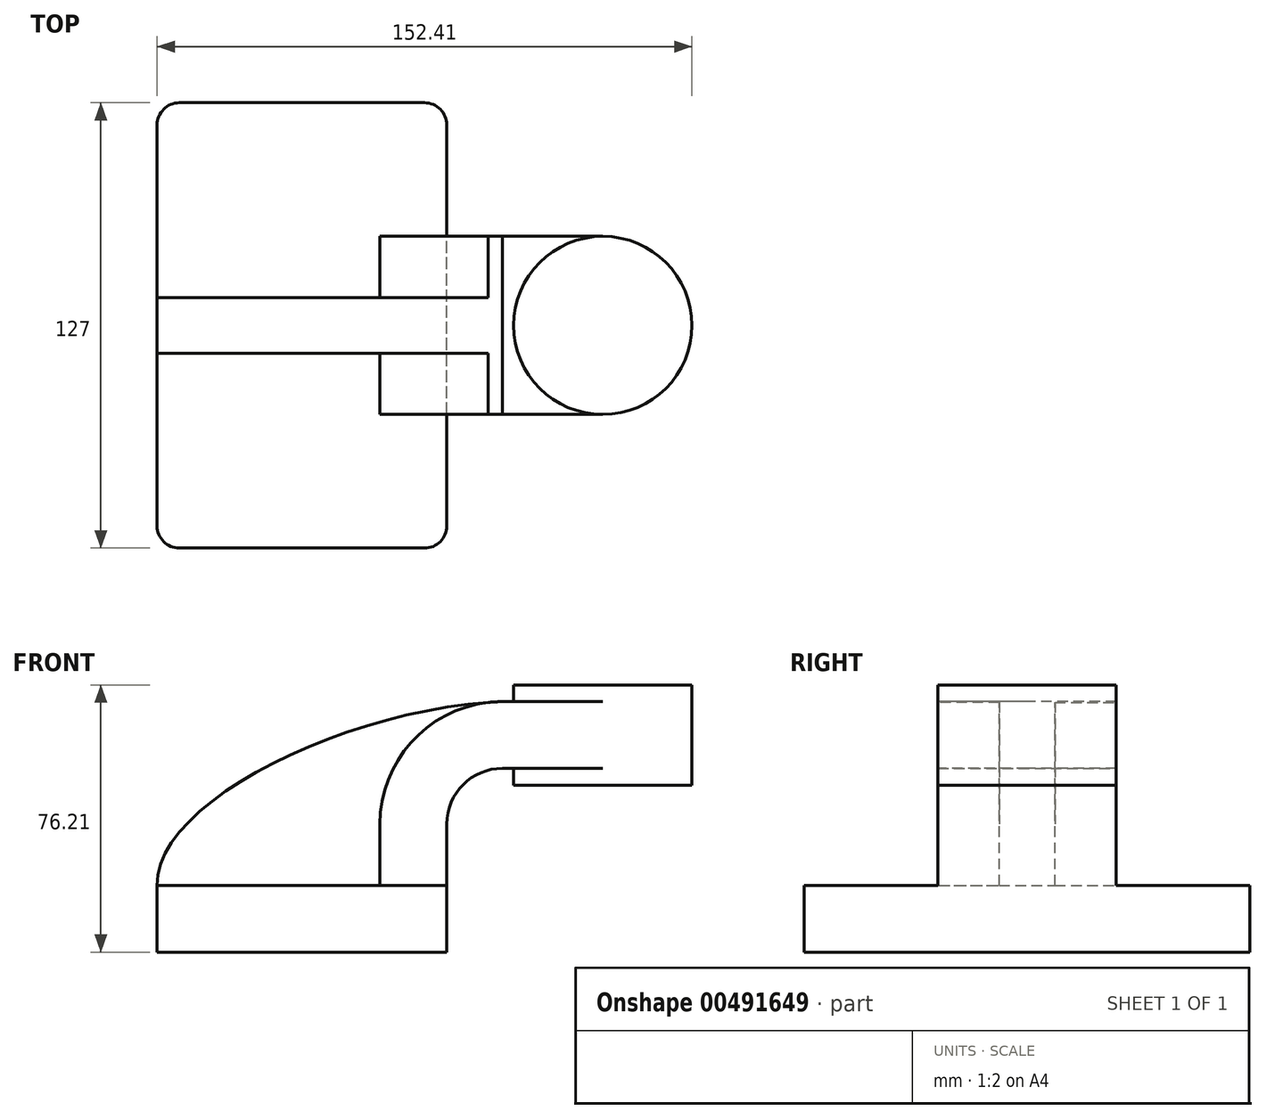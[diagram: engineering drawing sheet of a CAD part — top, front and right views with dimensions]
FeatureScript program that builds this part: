
annotation { "Feature Type Name" : "Feature", "Feature Type Description" : "" }
export const myFeature = defineFeature(function(context is Context, id is Id, definition is map)
    precondition{}
    {
        {
            var Q0;
            Q0=qCreatedBy(makeId("Front.planeOp"),FACE);
            var sketch = newSketch(context, id + "F0", { "sketchPlane" : qUnion([Q0])});
            skLineSegment(sketch, "E0.bottom", {"start": v(-41.28, 9.52) * mm, "end": v(41.27, 9.53) * mm});
            skLineSegment(sketch, "E0.top", {"start": v(-41.28, -9.53) * mm, "end": v(41.28, -9.53) * mm});
            skLineSegment(sketch, "E0.left", {"start": v(-41.28, 9.52) * mm, "end": v(-41.28, -9.53) * mm});
            skLineSegment(sketch, "E0.right", {"start": v(41.27, 9.53) * mm, "end": v(41.28, -9.52) * mm});
            skPoint(sketch, "E0.middle", {"position": v(0, 0) * mm});
            skLineSegment(sketch, "E1.bottom", {"start": v(60.32, 38.1) * mm, "end": v(111.12, 38.1) * mm});
            skLineSegment(sketch, "E1.top", {"start": v(60.32, 66.68) * mm, "end": v(111.12, 66.68) * mm});
            skLineSegment(sketch, "E1.left", {"start": v(60.32, 38.1) * mm, "end": v(60.32, 66.68) * mm});
            skLineSegment(sketch, "E1.right", {"start": v(111.12, 38.1) * mm, "end": v(111.12, 66.68) * mm});
            skPoint(sketch, "E1.middle", {"position": v(85.72, 52.39) * mm});
            skLineSegment(sketch, "E2", {"start": v(41.27, 9.53) * mm, "end": v(41.27, 27) * mm});
            skArc(sketch, "E3", {"start": v(41.27, 27) * mm, "mid": v(45.92, 38.23) * mm, "end": v(57.15, 42.88) * mm});
            skLineSegment(sketch, "E4", {"start": v(57.15, 42.88) * mm, "end": v(85.72, 42.88) * mm});
            skPoint(sketch, "E4.endSnap0", {"position": v(85.72, 38.1) * mm});
            skLineSegment(sketch, "E5.0", {"start": v(57.15, 61.93) * mm, "end": v(85.72, 61.93) * mm});
            skArc(sketch, "E5.1", {"start": v(22.22, 27) * mm, "mid": v(32.45, 51.7) * mm, "end": v(57.15, 61.93) * mm});
            skLineSegment(sketch, "E5.2", {"start": v(22.22, 9.53) * mm, "end": v(22.22, 27) * mm});
            skLineSegment(sketch, "E6", {"start": v(85.72, 38.1) * mm, "end": v(85.72, 66.68) * mm});
            skFitSpline(sketch, "E7", {"points": [v(-41.28, 9.52) * mm, v(57.15, 61.93) * mm], "startDerivative": vector(-1.75, 71.36) * mm, "endDerivative": vector(133.88, 5.67) * mm});
            skSolve(sketch);
        }
        {
            var Q0;
            Q0=makeQuery(id+"F0.imprint","IMPRINT",FACE,{"disambiguationData":[TD([[makeQuery(id+"F0.imprint","IMPRINT",EDGE,{"derivedFrom":sQuery(id+"F0.wireOp",EDGE,"E0.top")}),1.0]])]});
            extrude(context, id + "F1", {"entities" : qUnion([Q0]), "endBound" : BoundingType.SYMMETRIC, "depth" : 127 * mm});
        }
        {
            var Q0;
            {var subQ1=sQuery(id+"F0.wireOp",EDGE,"E2");Q0=makeQuery(id+"F0.imprint","IMPRINT",FACE,{"disambiguationData":[TD([[makeQuery(id+"F0.imprint","IMPRINT",EDGE,{"derivedFrom":subQ1}),1.0]])]});}
            var Q1;
            {var subQ0=sQuery(id+"F0.wireOp",EDGE,"E4");var subQ1=sQuery(id+"F0.wireOp",EDGE,"E1.left");var subQ2=makeQuery(id+"F0.imprint","INTERSECT",VERTEX,{"derivedFrom":[subQ1,subQ0]});Q1=makeQuery(id+"F0.imprint","IMPRINT",FACE,{"disambiguationData":[TD([[makeQuery(id+"F0.imprint","IMPRINT",EDGE,{"disambiguationData":[TD([[subQ2,-1.0]])],"derivedFrom":subQ1}),-1.0]])]});}
            extrude(context, id + "F2", {"entities" : qUnion([Q0, Q1]), "operationType" : NewBodyOperationType.ADD, "endBound" : BoundingType.SYMMETRIC, "depth" : 50.8 * mm});
        }
        {
            var Q0;
            {var subQ3=sQuery(id+"F0.wireOp",EDGE,"E5.2");Q0=makeQuery(id+"F0.imprint","IMPRINT",FACE,{"disambiguationData":[TD([[makeQuery(id+"F0.imprint","IMPRINT",EDGE,{"derivedFrom":subQ3}),1.0]])]});}
            extrude(context, id + "F3", {"entities" : qUnion([Q0]), "operationType" : NewBodyOperationType.ADD, "endBound" : BoundingType.SYMMETRIC, "depth" : 15.88 * mm});
        }
        {
            var Q0;
            {var subQ4=sQuery(id+"F0.wireOp",EDGE,"E1.right");Q0=makeQuery(id+"F0.imprint","IMPRINT",FACE,{"disambiguationData":[TD([[makeQuery(id+"F0.imprint","IMPRINT",EDGE,{"derivedFrom":subQ4}),1.0]])]});}
            var Q1;
            Q1=sQuery(id+"F0.wireOp",EDGE,"E6");
            revolve(context, id + "F4", {"operationType" : NewBodyOperationType.ADD, "entities" : qUnion([Q0]), "axis" : qUnion([Q1]), "revolveType" : RevolveType.FULL});
        }
        {
            var Q0;
            Q0=makeQuery(id+"F1.opExtrude","CAP_EDGE",EDGE,{"disambiguationData":[OSD([sQuery(id+"F0.wireOp",EDGE,"E0.left")])],"isStart":false});
            var Q1;
            Q1=makeQuery(id+"F1.opExtrude","CAP_EDGE",EDGE,{"disambiguationData":[OSD([sQuery(id+"F0.wireOp",EDGE,"E0.right")])],"isStart":false});
            var Q2;
            Q2=makeQuery(id+"F1.opExtrude","CAP_EDGE",EDGE,{"disambiguationData":[OSD([sQuery(id+"F0.wireOp",EDGE,"E0.right")])],"isStart":true});
            var Q3;
            Q3=makeQuery(id+"F1.opExtrude","CAP_EDGE",EDGE,{"disambiguationData":[OSD([sQuery(id+"F0.wireOp",EDGE,"E0.left")])],"isStart":true});
            fillet(context, id + "F5", {"entities" : qUnion([Q0, Q1, Q2, Q3]), "radius" : 6.35 * mm, "tangentPropagation" : true, "allowEdgeOverflow" : false});
        }
    });
